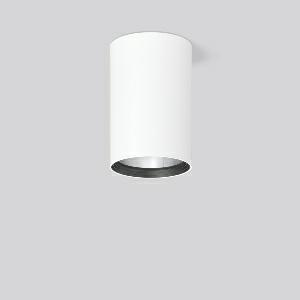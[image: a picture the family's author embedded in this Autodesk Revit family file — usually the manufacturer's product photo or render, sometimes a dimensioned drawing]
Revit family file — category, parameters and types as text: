
# Revit family: heledon_maxi_a_931218_002_3_e7f3
name_source: partatom
category: Lighting Fixtures
units: mm (PartAtom-declared; Revit-internal decimal feet)

## family parameters
Cut with Voids When Loaded = No
Host = Face
Light Source = No
Part Type = Normal
Room Calculation Point = No
Round Connector Dimension = Use Diameter
Shared = No

## types (1)
- HELEDON maxi A (1 x LED Modul 935, 3400 lm, 3500)
    Apparent Load = 25 VA
    Approval mark = CE
    CIE Flux Codes = 100 100 100 100 100
    Color Rendering = 92
    Color Temperature = 3500
    Default Elevation = 1800 mm
    Description = Series: HELEDON maxi
Cylindrical surface-mounted downlight. Housing: die-cast aluminium, powder-coated. Internal ceiling frame polycarbonate with bayonet mounting. Black plastic ring and recessed LED to prevent glare from the side. Optical assembly with reflector made of MIRO-Silver with 98% total light reflection for outstanding efficiency - can be changed without tools. Best colour rendering index Ra>90. Suitable for Ceiling mounting. Easy installation with a separate ceiling frame with bayonet mounting and plug connection. Driver integrated. Connected via plug-in connector. High quality converter without flickering and stroboscopic effect. The following accessories can be mounted without use of tools: interchangeable lenses, decorative glasses, honeycomb louvre, clear and frosted diffusers, white interchangeable plastic ring. 
Colour: traffic white, matt (RAL 9016)
Diameter: 123 mm
Height: 183 mm
Lamp: LED
Socket: without socket
Colour temperature: 3500K
Colour rendering index (CRI): 92
System power: 25 W
Rated luminous flux: 3400 lm
Luminous efficiency: 136 lm/W
Control gear: Regulated power supply
Protection class: I
Type of protection: IP 20
    Height = 183 mm
    Lamp = 1 x LED Modul 935
    Lamp Light Flux = 3400 lm
    Lamp count = 1
    Length = 123 mm
    Lifetime = 50000 h
    Luminous efficacy = 136 lm/W
    Manufacturer = RZB
    ModVariant = No
    Model = 931218.002.3
    Mounting Place = Ceiling
    Mounting Type = Surface mounted
    Number of Poles = 1
    OnlyDefault = Yes
    Power Factor = 1
    Product Name = HELEDON maxi A
    Product group = Surface mounted downlights
    ProductGroupID = 302
    Protection Class = Protection class I
    Protection Degree = IP 20
    RLX_Detail_Level = 1
    RLX_Emergency_Light_Flux = 0 lm
    RLX_Emergency_Type = 0
    RLX_Emergency_Type_DB = No
    RlxData = <blob elided: 99249 chars, md5=0a9ca110>
    Socket = socket
    Standby Power = 0 W
    System Light Flux = 3400 lm
    System Power = 25 W
    Type Comments = Product without accessories
    Type Image = 931192.002.jpg
    URL = http://relux.com
    VarID = ---
    Voltage = 230 V
    Voltage Range = 220-240 V
    Weight = 0.00 kg
    Width = 0 mm  [stored 0 ft]

note: [stored X ft] marks values corroborated as IEEE doubles in the binary element streams (Revit-internal decimal feet)

## geometry (parser evidence)
native form markers: Blend x4, Sweep x11
no freeform markers — native parametric forms only
